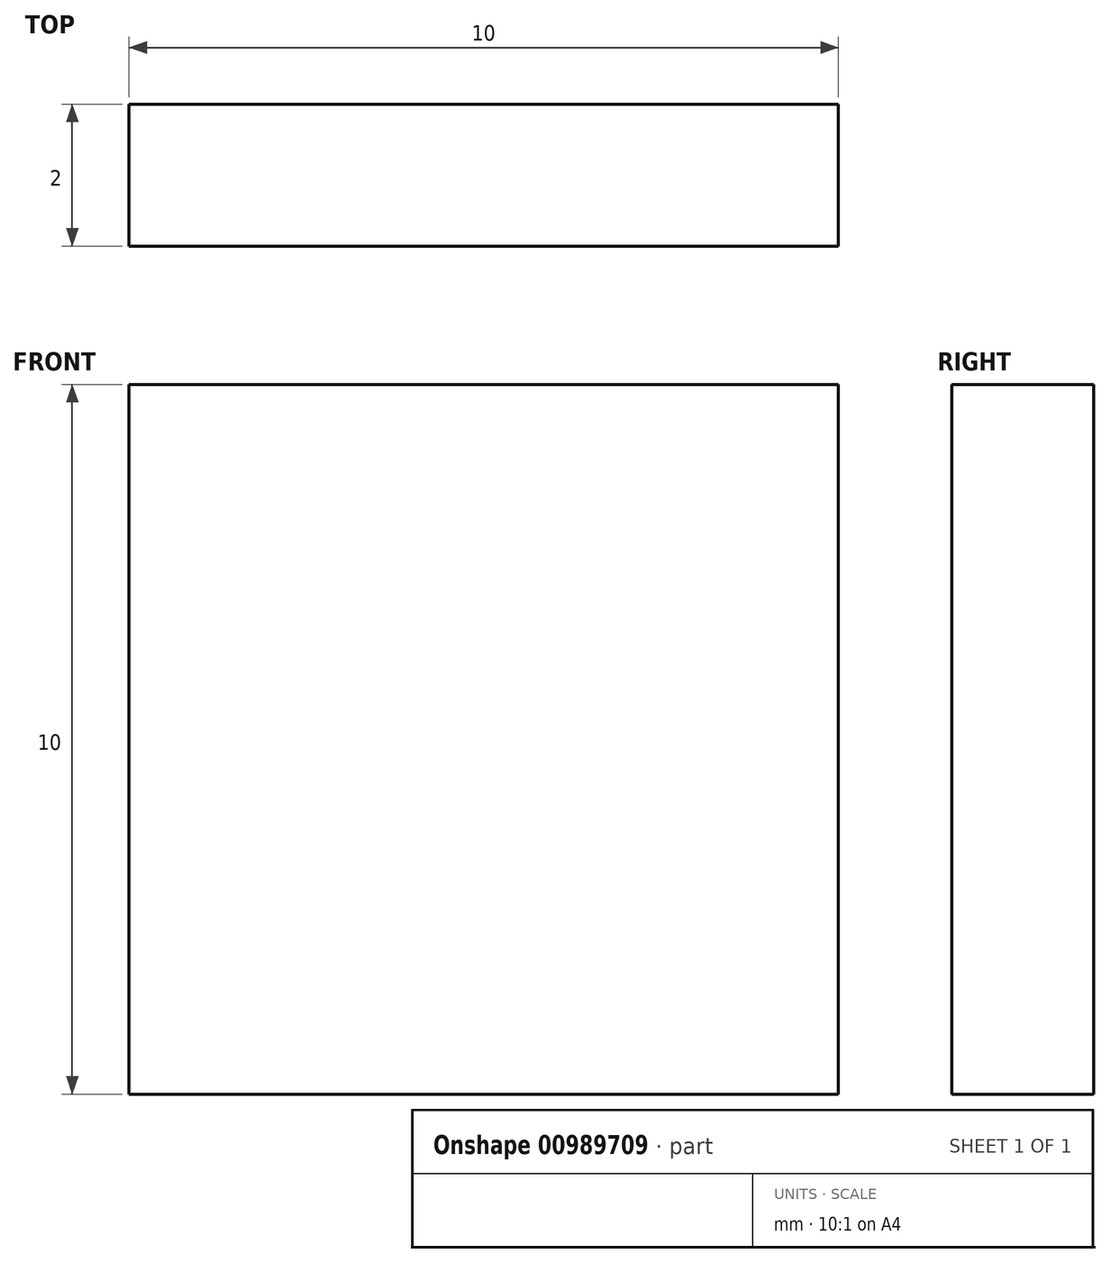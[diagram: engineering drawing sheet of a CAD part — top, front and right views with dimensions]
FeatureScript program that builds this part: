
annotation { "Feature Type Name" : "Feature", "Feature Type Description" : "" }
export const myFeature = defineFeature(function(context is Context, id is Id, definition is map)
    precondition{}
    {
        {
            var Q0;
            Q0=qCreatedBy(makeId("Front.planeOp"),FACE);
            var sketch = newSketch(context, id + "F0", { "sketchPlane" : qUnion([Q0])});
            skLineSegment(sketch, "E0.bottom", {"start": v(0, 0) * mm, "end": v(10, 0) * mm});
            skLineSegment(sketch, "E0.top", {"start": v(0, 10) * mm, "end": v(10, 10) * mm});
            skLineSegment(sketch, "E0.left", {"start": v(0, 0) * mm, "end": v(0, 10) * mm});
            skLineSegment(sketch, "E0.right", {"start": v(10, 0) * mm, "end": v(10, 10) * mm});
            skSolve(sketch);
        }
        {
            var Q0;
            Q0 = qSketchRegion(id + "F0", true);
            extrude(context, id + "F1", {"entities" : qUnion([Q0]), "endBound" : BoundingType.SYMMETRIC, "depth" : 2 * mm, "offsetDistance" : 25 * mm});
        }
    });
